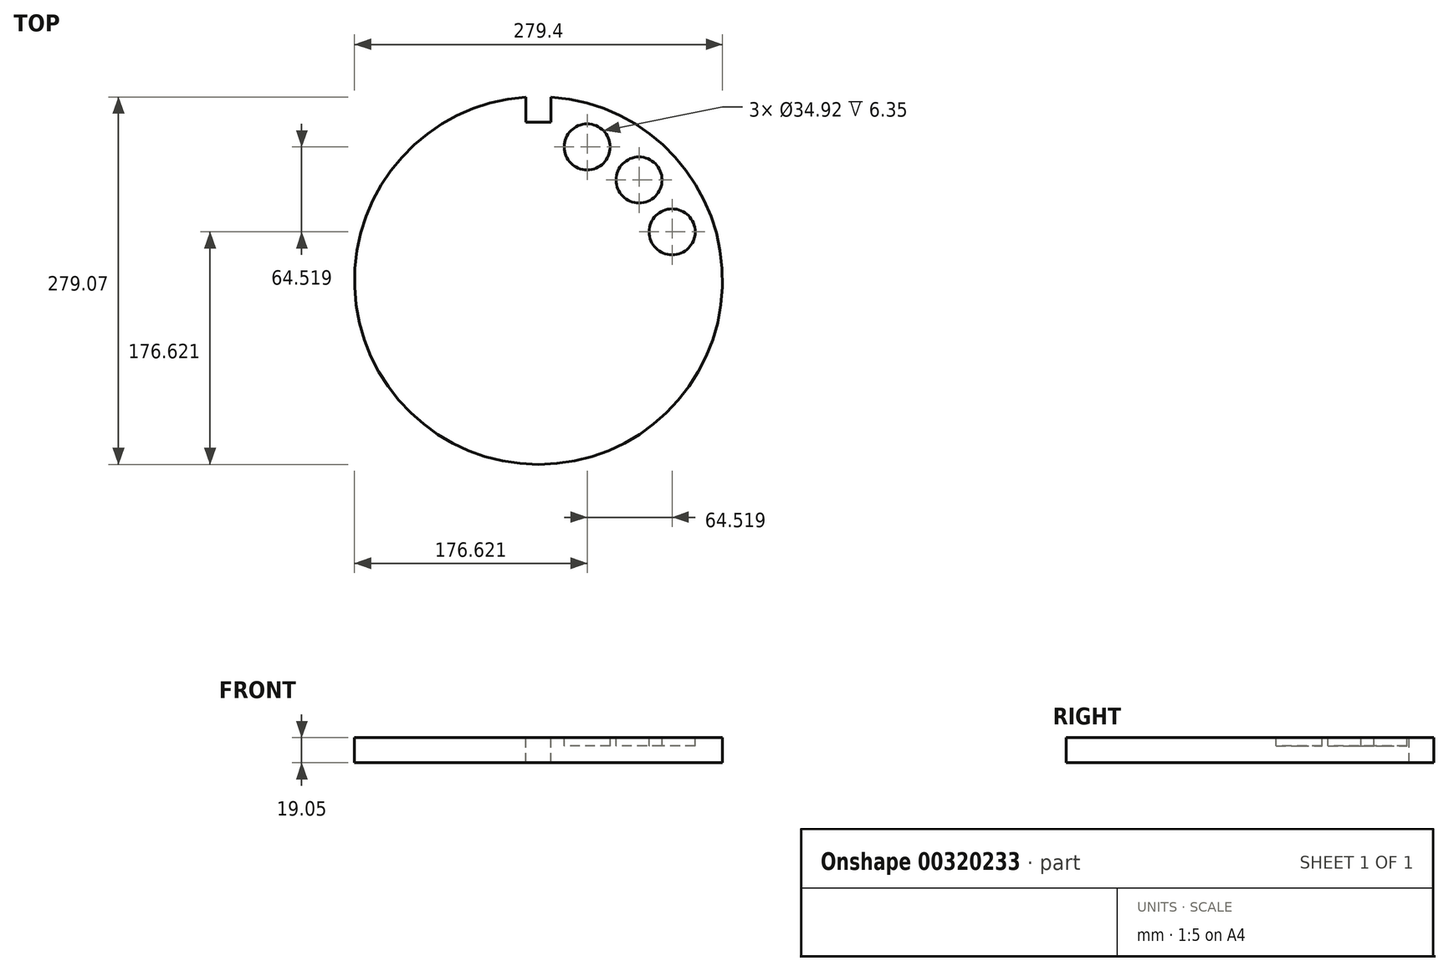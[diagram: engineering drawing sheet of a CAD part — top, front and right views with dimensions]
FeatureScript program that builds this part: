
annotation { "Feature Type Name" : "Feature", "Feature Type Description" : "" }
export const myFeature = defineFeature(function(context is Context, id is Id, definition is map)
    precondition{}
    {
        {
            var Q0;
            Q0=qCreatedBy(makeId("Top.planeOp"),FACE);
            var sketch = newSketch(context, id + "F0", { "sketchPlane" : qUnion([Q0])});
            skCircle(sketch, "E0", {"center": v(0, 0) * mm, "radius": 107.95 * mm, "construction": true});
            skCircle(sketch, "E1", {"center": v(0, 0) * mm, "radius": 139.7 * mm});
            skLineSegment(sketch, "E2", {"start": v(0, 0) * mm, "end": v(139.7, 0) * mm, "construction": true});
            skLineSegment(sketch, "E3", {"start": v(0, 0) * mm, "end": v(0, 139.7) * mm, "construction": true});
            skLineSegment(sketch, "E4", {"start": v(0, 0) * mm, "end": v(76.33, 76.33) * mm, "construction": true});
            skLineSegment(sketch, "E5", {"start": v(0, 0) * mm, "end": v(101.44, 36.92) * mm, "construction": true});
            skLineSegment(sketch, "E6", {"start": v(0, 0) * mm, "end": v(36.92, 101.44) * mm, "construction": true});
            skCircle(sketch, "E7", {"center": v(36.92, 101.44) * mm, "radius": 17.46 * mm});
            skCircle(sketch, "E8", {"center": v(76.33, 76.33) * mm, "radius": 17.46 * mm});
            skCircle(sketch, "E9", {"center": v(101.44, 36.92) * mm, "radius": 17.46 * mm});
            skLineSegment(sketch, "E10.top", {"start": v(-9.53, 113.97) * mm, "end": v(9.52, 113.97) * mm});
            skLineSegment(sketch, "E10.left", {"start": v(-9.53, 139.37) * mm, "end": v(-9.53, 113.97) * mm});
            skLineSegment(sketch, "E10.right", {"start": v(9.52, 139.37) * mm, "end": v(9.52, 113.97) * mm});
            skPoint(sketch, "E10.middle", {"position": v(0, 126.67) * mm});
            skLineSegment(sketch, "E11", {"start": v(-9.53, 120.32) * mm, "end": v(9.52, 120.32) * mm});
            skSolve(sketch);
        }
        {
            var Q0;
            Q0=qSketchRegion(id+"F0",true);
            var Q1;
            Q1=makeQuery(id+"F0.imprint","IMPRINT",FACE,{"disambiguationData":[TD([[makeQuery(id+"F0.imprint","IMPRINT",EDGE,{"derivedFrom":sQuery(id+"F0.wireOp",EDGE,"E7")}),1.0]])]});
            var Q2;
            Q2=makeQuery(id+"F0.imprint","IMPRINT",FACE,{"disambiguationData":[TD([[makeQuery(id+"F0.imprint","IMPRINT",EDGE,{"derivedFrom":sQuery(id+"F0.wireOp",EDGE,"E8")}),1.0]])]});
            var Q3;
            Q3=makeQuery(id+"F0.imprint","IMPRINT",FACE,{"disambiguationData":[TD([[makeQuery(id+"F0.imprint","IMPRINT",EDGE,{"derivedFrom":sQuery(id+"F0.wireOp",EDGE,"E9")}),1.0]])]});
            var Q4;
            {var subQ0=sQuery(id+"F0.wireOp",EDGE,"E10.top");Q4=makeQuery(id+"F0.imprint","IMPRINT",FACE,{"disambiguationData":[TD([[makeQuery(id+"F0.imprint","IMPRINT",EDGE,{"derivedFrom":subQ0}),1.0]])]});}
            extrude(context, id + "F1", {"entities" : qUnion([Q0, Q1, Q2, Q3, Q4]), "oppositeDirection" : true, "depth" : 19.05 * mm});
        }
        {
            var Q0;
            Q0=makeQuery(id+"F0.imprint","IMPRINT",FACE,{"disambiguationData":[TD([[makeQuery(id+"F0.imprint","IMPRINT",EDGE,{"derivedFrom":sQuery(id+"F0.wireOp",EDGE,"E7")}),1.0]])]});
            var Q1;
            Q1=makeQuery(id+"F0.imprint","IMPRINT",FACE,{"disambiguationData":[TD([[makeQuery(id+"F0.imprint","IMPRINT",EDGE,{"derivedFrom":sQuery(id+"F0.wireOp",EDGE,"E8")}),1.0]])]});
            var Q2;
            Q2=makeQuery(id+"F0.imprint","IMPRINT",FACE,{"disambiguationData":[TD([[makeQuery(id+"F0.imprint","IMPRINT",EDGE,{"derivedFrom":sQuery(id+"F0.wireOp",EDGE,"E9")}),1.0]])]});
            extrude(context, id + "F2", {"entities" : qUnion([Q0, Q1, Q2]), "operationType" : NewBodyOperationType.REMOVE, "oppositeDirection" : true, "depth" : 6.35 * mm});
        }
        {
            var Q0;
            {var subQ5=sQuery(id+"F0.wireOp",EDGE,"E11");Q0=makeQuery(id+"F0.imprint","IMPRINT",FACE,{"disambiguationData":[TD([[makeQuery(id+"F0.imprint","IMPRINT",EDGE,{"derivedFrom":subQ5}),1.0]])]});}
            extrude(context, id + "F3", {"entities" : qUnion([Q0]), "operationType" : NewBodyOperationType.REMOVE, "endBound" : BoundingType.THROUGH_ALL, "oppositeDirection" : true, "depth" : 25.4 * mm});
        }
        {
            var Q0;
            Q0=qCreatedBy(makeId("Front.planeOp"),FACE);
            var sketch = newSketch(context, id + "F4", { "sketchPlane" : qUnion([Q0])});
            skLineSegment(sketch, "E12", {"start": v(0, 0) * mm, "end": v(0, 89.72) * mm, "construction": true});
            skSolve(sketch);
        }
    });
